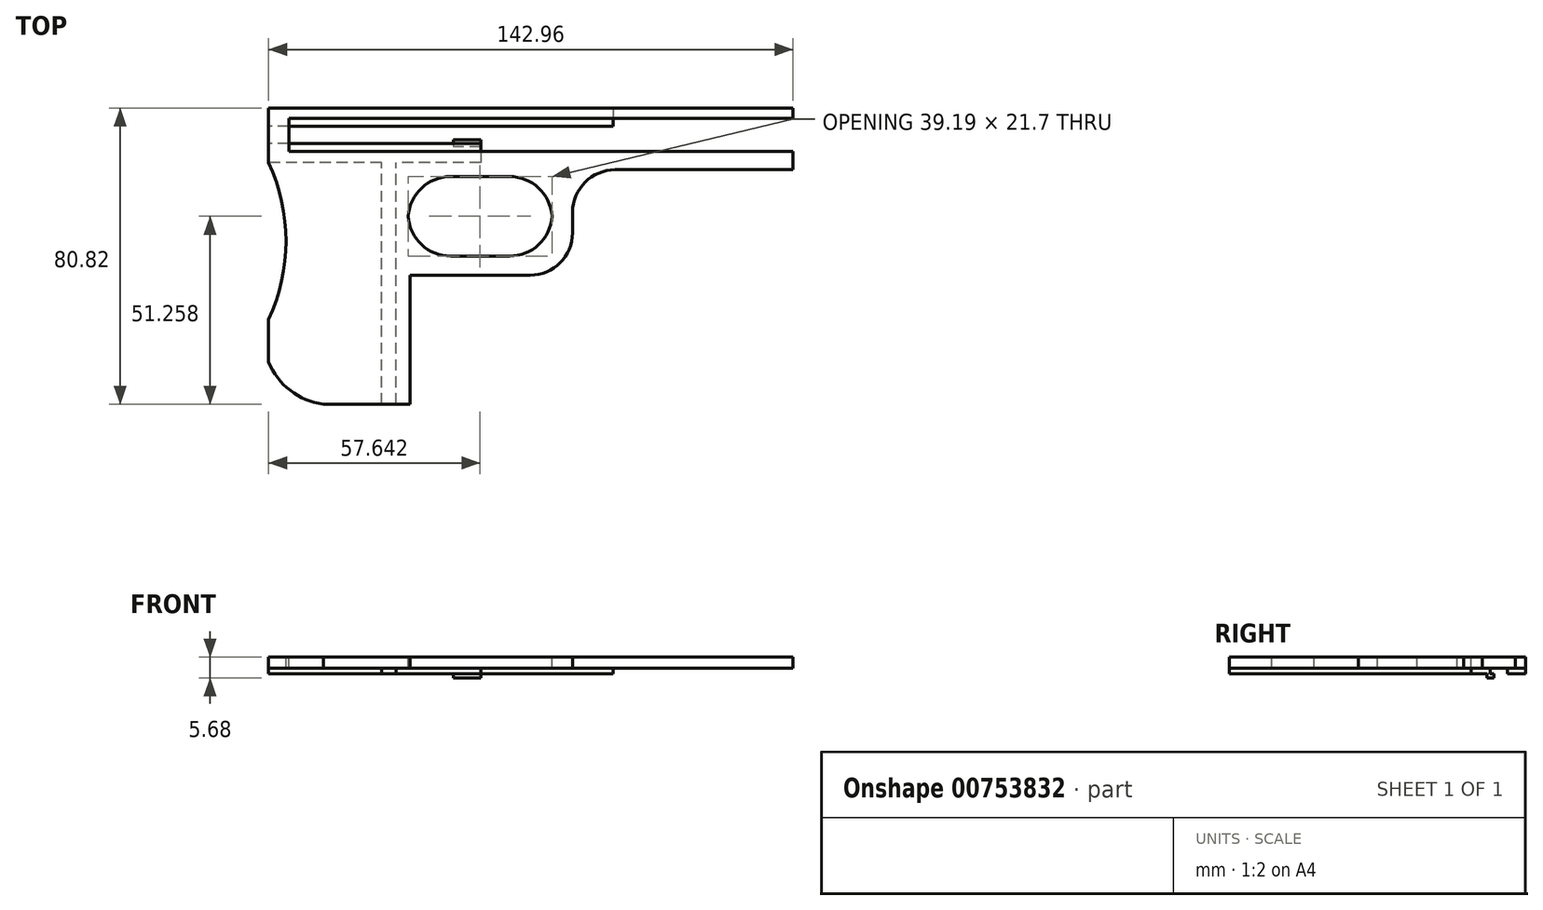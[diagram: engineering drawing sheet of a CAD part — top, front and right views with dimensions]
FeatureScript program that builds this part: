
annotation { "Feature Type Name" : "Feature", "Feature Type Description" : "" }
export const myFeature = defineFeature(function(context is Context, id is Id, definition is map)
    precondition{}
    {
        {
            var Q0;
            Q0=qCreatedBy(makeId("Top.planeOp"),FACE);
            var sketch = newSketch(context, id + "F0", { "sketchPlane" : qUnion([Q0])});
            skLineSegment(sketch, "E0.bottom", {"start": v(-71.48, -40.4) * mm, "end": v(71.48, -40.4) * mm});
            skLineSegment(sketch, "E0.top", {"start": v(-71.48, 40.4) * mm, "end": v(71.48, 40.4) * mm});
            skLineSegment(sketch, "E0.left", {"start": v(-71.48, -40.4) * mm, "end": v(-71.48, 40.4) * mm});
            skLineSegment(sketch, "E0.right", {"start": v(71.48, -40.4) * mm, "end": v(71.48, 40.4) * mm});
            skPoint(sketch, "E0.middle", {"position": v(0, 0) * mm});
            skSolve(sketch);
        }
        {
            var Q0;
            Q0 = qSketchRegion(id + "F0", true);
            extrude(context, id + "F1", {"entities" : qUnion([Q0]), "depth" : 3 * mm, "offsetDistance" : 25 * mm});
        }
        {
            var Q0;
            Q0=makeQuery(id+"F1.opExtrude","CAP_FACE",FACE,{"disambiguationData":[OSD([sQuery(id+"F0.wireOp",EDGE,"E0.bottom"),sQuery(id+"F0.wireOp",EDGE,"E0.top"),sQuery(id+"F0.wireOp",EDGE,"E0.left"),sQuery(id+"F0.wireOp",EDGE,"E0.right")])],"isStart":false});
            var sketch = newSketch(context, id + "F2", { "sketchPlane" : qUnion([Q0])});
            skLineSegment(sketch, "E1.bottom", {"start": v(-65.97, 37.55) * mm, "end": v(71.48, 37.55) * mm});
            skLineSegment(sketch, "E1.top", {"start": v(-65.97, 28.57) * mm, "end": v(71.48, 28.57) * mm});
            skLineSegment(sketch, "E1.left", {"start": v(-65.97, 37.55) * mm, "end": v(-65.97, 28.57) * mm});
            skLineSegment(sketch, "E1.right", {"start": v(71.48, 37.55) * mm, "end": v(71.48, 28.57) * mm});
            skLineSegment(sketch, "E2.bottom", {"start": v(71.48, 23.55) * mm, "end": v(11.39, 23.55) * mm});
            skLineSegment(sketch, "E2.top", {"start": v(71.48, 5.05) * mm, "end": v(11.39, 5.05) * mm});
            skLineSegment(sketch, "E2.left", {"start": v(71.48, 23.55) * mm, "end": v(71.48, 5.05) * mm});
            skLineSegment(sketch, "E2.right", {"start": v(11.39, 23.55) * mm, "end": v(11.39, 5.05) * mm});
            skSolve(sketch);
        }
        {
            var Q0;
            Q0 = qSketchRegion(id + "F2", true);
            extrude(context, id + "F3", {"entities" : qUnion([Q0]), "operationType" : NewBodyOperationType.REMOVE, "oppositeDirection" : true, "depth" : 52.3 * mm, "offsetDistance" : 25 * mm});
        }
        {
            var Q0;
            Q0=makeQuery(id+"F1.opExtrude","CAP_FACE",FACE,{"disambiguationData":[OSD([sQuery(id+"F0.wireOp",EDGE,"E0.bottom"),sQuery(id+"F0.wireOp",EDGE,"E0.top"),sQuery(id+"F0.wireOp",EDGE,"E0.left"),sQuery(id+"F0.wireOp",EDGE,"E0.right")])],"isStart":false});
            var sketch = newSketch(context, id + "F4", { "sketchPlane" : qUnion([Q0])});
            skLineSegment(sketch, "E3.bottom", {"start": v(-33.46, 21.7) * mm, "end": v(5.78, 21.7) * mm});
            skLineSegment(sketch, "E3.top", {"start": v(-33.46, 0) * mm, "end": v(5.78, 0) * mm});
            skLineSegment(sketch, "E3.left", {"start": v(-33.46, 21.7) * mm, "end": v(-33.46, 0) * mm});
            skLineSegment(sketch, "E3.right", {"start": v(5.78, 21.7) * mm, "end": v(5.78, 0) * mm});
            skSolve(sketch);
        }
        {
            var Q0;
            Q0 = qSketchRegion(id + "F4", true);
            extrude(context, id + "F5", {"entities" : qUnion([Q0]), "operationType" : NewBodyOperationType.REMOVE, "oppositeDirection" : true, "depth" : 25 * mm, "offsetDistance" : 25 * mm});
        }
        {
            var Q0;
            Q0=makeQuery(id+"F1.opExtrude","CAP_FACE",FACE,{"disambiguationData":[OSD([sQuery(id+"F0.wireOp",EDGE,"E0.bottom"),sQuery(id+"F0.wireOp",EDGE,"E0.top"),sQuery(id+"F0.wireOp",EDGE,"E0.left"),sQuery(id+"F0.wireOp",EDGE,"E0.right")])],"isStart":false});
            var sketch = newSketch(context, id + "F6", { "sketchPlane" : qUnion([Q0])});
            skLineSegment(sketch, "E4.bottom", {"start": v(13.75, 0) * mm, "end": v(98.67, 0) * mm});
            skLineSegment(sketch, "E4.top", {"start": v(13.75, -55.24) * mm, "end": v(98.67, -55.24) * mm});
            skLineSegment(sketch, "E4.left", {"start": v(13.75, 0) * mm, "end": v(13.75, -55.24) * mm});
            skLineSegment(sketch, "E4.right", {"start": v(98.67, 0) * mm, "end": v(98.67, -55.24) * mm});
            skLineSegment(sketch, "E5.bottom", {"start": v(17.1, -5.2) * mm, "end": v(-27.22, -5.2) * mm});
            skLineSegment(sketch, "E5.top", {"start": v(17.1, -49.97) * mm, "end": v(-27.22, -49.97) * mm});
            skLineSegment(sketch, "E5.left", {"start": v(17.1, -5.2) * mm, "end": v(17.1, -49.97) * mm});
            skLineSegment(sketch, "E5.right", {"start": v(-27.22, -5.2) * mm, "end": v(-27.22, -49.97) * mm});
            skSolve(sketch);
        }
        {
            var Q0;
            Q0 = qSketchRegion(id + "F6", true);
            extrude(context, id + "F7", {"entities" : qUnion([Q0]), "operationType" : NewBodyOperationType.REMOVE, "oppositeDirection" : true, "depth" : 25 * mm, "offsetDistance" : 25 * mm});
        }
        {
            var Q0;
            Q0=makeQuery(id+"F1.opExtrude","CAP_FACE",FACE,{"disambiguationData":[OSD([sQuery(id+"F0.wireOp",EDGE,"E0.bottom"),sQuery(id+"F0.wireOp",EDGE,"E0.top"),sQuery(id+"F0.wireOp",EDGE,"E0.left"),sQuery(id+"F0.wireOp",EDGE,"E0.right")])],"isStart":false});
            var sketch = newSketch(context, id + "F8", { "sketchPlane" : qUnion([Q0])});
            skLineSegment(sketch, "E6.bottom", {"start": v(11.39, 5.05) * mm, "end": v(114, 5.05) * mm});
            skLineSegment(sketch, "E6.top", {"start": v(11.39, -13.38) * mm, "end": v(114, -13.38) * mm});
            skLineSegment(sketch, "E6.left", {"start": v(11.39, 5.05) * mm, "end": v(11.39, -13.38) * mm});
            skLineSegment(sketch, "E6.right", {"start": v(114, 5.05) * mm, "end": v(114, -13.38) * mm});
            skSolve(sketch);
        }
        {
            var Q0;
            Q0 = qSketchRegion(id + "F8", true);
            extrude(context, id + "F9", {"entities" : qUnion([Q0]), "operationType" : NewBodyOperationType.REMOVE, "oppositeDirection" : true, "depth" : 25 * mm, "offsetDistance" : 25 * mm});
        }
        {
            var Q0;
            Q0=makeQuery(id+"F9.boolean.opBoolean","INTERSECT",EDGE,{"derivedFrom":[makeQuery(id+"F7.boolean.opBoolean","COPY",FACE,{"derivedFrom":makeQuery(id+"F7.opExtrude","SWEPT_FACE",FACE,{"disambiguationData":[OSD([sQuery(id+"F6.wireOp",EDGE,"E5.bottom")])]})}),makeQuery(id+"F9.opExtrude","SWEPT_FACE",FACE,{"disambiguationData":[OSD([sQuery(id+"F8.wireOp",EDGE,"E6.left")])]})]});
            var Q1;
            Q1=makeQuery(id+"F3.boolean.opBoolean","COPY",EDGE,{"derivedFrom":makeQuery(id+"F3.opExtrude","SWEPT_EDGE",EDGE,{"disambiguationData":[OSD([sQuery(id+"F2.wireOp",EDGE,"E2.bottom"),sQuery(id+"F2.wireOp",EDGE,"E2.right")])]})});
            var Q2;
            Q2=makeQuery(id+"F7.boolean.opBoolean","COPY",EDGE,{"derivedFrom":makeQuery(id+"F7.opExtrude","SWEPT_EDGE",EDGE,{"disambiguationData":[OSD([sQuery(id+"F6.wireOp",EDGE,"E5.bottom"),sQuery(id+"F6.wireOp",EDGE,"E5.right")])]})});
            var Q3;
            Q3=makeQuery(id+"F5.boolean.opBoolean","COPY",EDGE,{"derivedFrom":makeQuery(id+"F5.opExtrude","SWEPT_EDGE",EDGE,{"disambiguationData":[OSD([sQuery(id+"F4.wireOp",EDGE,"E3.bottom"),sQuery(id+"F4.wireOp",EDGE,"E3.left")])]})});
            var Q4;
            Q4=makeQuery(id+"F5.boolean.opBoolean","COPY",EDGE,{"derivedFrom":makeQuery(id+"F5.opExtrude","SWEPT_EDGE",EDGE,{"disambiguationData":[OSD([sQuery(id+"F4.wireOp",EDGE,"E3.top"),sQuery(id+"F4.wireOp",EDGE,"E3.right")])]})});
            var Q5;
            Q5=makeQuery(id+"F5.boolean.opBoolean","COPY",EDGE,{"derivedFrom":makeQuery(id+"F5.opExtrude","SWEPT_EDGE",EDGE,{"disambiguationData":[OSD([sQuery(id+"F4.wireOp",EDGE,"E3.top"),sQuery(id+"F4.wireOp",EDGE,"E3.left")])]})});
            var Q6;
            Q6=makeQuery(id+"F5.boolean.opBoolean","COPY",EDGE,{"derivedFrom":makeQuery(id+"F5.opExtrude","SWEPT_EDGE",EDGE,{"disambiguationData":[OSD([sQuery(id+"F4.wireOp",EDGE,"E3.bottom"),sQuery(id+"F4.wireOp",EDGE,"E3.right")])]})});
            fillet(context, id + "F10", {"entities" : qUnion([Q0, Q1, Q2, Q3, Q4, Q5, Q6]), "radius" : 11.6 * mm, "tangentPropagation" : true, "allowEdgeOverflow" : false});
        }
        {
            var Q0;
            Q0=makeQuery(id+"F1.opExtrude","CAP_FACE",FACE,{"disambiguationData":[OSD([sQuery(id+"F0.wireOp",EDGE,"E0.bottom"),sQuery(id+"F0.wireOp",EDGE,"E0.top"),sQuery(id+"F0.wireOp",EDGE,"E0.left"),sQuery(id+"F0.wireOp",EDGE,"E0.right")])],"isStart":false});
            var sketch = newSketch(context, id + "F11", { "sketchPlane" : qUnion([Q0])});
            skArc(sketch, "E7", {"start": v(-71.48, -17.3) * mm, "mid": v(-66.77, 4.1) * mm, "end": v(-71.48, 25.5) * mm});
            skSolve(sketch);
        }
        {
            var Q0;
            Q0 = qSketchRegion(id + "F11", true);
            var Q1;
            {var subQ0=sQuery(id+"F11.wireOp",EDGE,"E7");Q1=makeQuery(id+"F11.imprint","IMPRINT",FACE,{"disambiguationData":[TD([[makeQuery(id+"F11.imprint","IMPRINT",EDGE,{"derivedFrom":subQ0}),1.0]])]});}
            extrude(context, id + "F12", {"entities" : qUnion([Q0, Q1]), "operationType" : NewBodyOperationType.REMOVE, "oppositeDirection" : true, "depth" : 25 * mm, "offsetDistance" : 25 * mm});
        }
        {
            var Q0;
            Q0=makeQuery(id+"F1.opExtrude","CAP_FACE",FACE,{"disambiguationData":[OSD([sQuery(id+"F0.wireOp",EDGE,"E0.bottom"),sQuery(id+"F0.wireOp",EDGE,"E0.top"),sQuery(id+"F0.wireOp",EDGE,"E0.left"),sQuery(id+"F0.wireOp",EDGE,"E0.right")])],"isStart":false});
            var sketch = newSketch(context, id + "F13", { "sketchPlane" : qUnion([Q0])});
            skArc(sketch, "E8", {"start": v(-71.48, -28.86) * mm, "mid": v(-63.55, -38.02) * mm, "end": v(-51.66, -40.4) * mm});
            skArc(sketch, "E9", {"start": v(-32.9, -40.4) * mm, "mid": v(-27.36, -33.24) * mm, "end": v(-27.22, -24.18) * mm});
            skArc(sketch, "E10", {"start": v(-21.32, -6.7) * mm, "mid": v(-30.12, -13.47) * mm, "end": v(-27.22, -24.18) * mm});
            skSolve(sketch);
        }
        {
            var Q0;
            {var subQ0=sQuery(id+"F13.wireOp",EDGE,"E10");Q0=makeQuery(id+"F13.imprint","IMPRINT",FACE,{"disambiguationData":[TD([[makeQuery(id+"F13.imprint","IMPRINT",EDGE,{"derivedFrom":subQ0}),1.0]])]});}
            var Q1;
            {var subQ0=sQuery(id+"F13.wireOp",EDGE,"E9");var subQ1=makeQuery(id+"F1.opExtrude","CAP_EDGE",EDGE,{"disambiguationData":[OSD([sQuery(id+"F0.wireOp",EDGE,"E0.bottom")])],"isStart":false});var subQ2=makeQuery(id+"F13.imprint","INTERSECT",VERTEX,{"derivedFrom":[subQ1,subQ0]});Q1=makeQuery(id+"F13.imprint","IMPRINT",FACE,{"disambiguationData":[TD([[makeQuery(id+"F13.imprint","IMPRINT",EDGE,{"disambiguationData":[TD([[subQ2,-1.0]])],"derivedFrom":subQ0}),-1.0]])]});}
            var Q2;
            {var subQ0=sQuery(id+"F13.wireOp",EDGE,"E8");var subQ1=sQuery(id+"F0.wireOp",EDGE,"E0.bottom");var subQ5=makeQuery(id+"F1.opExtrude","CAP_EDGE",EDGE,{"disambiguationData":[OSD([subQ1])],"isStart":false});var subQ6=makeQuery(id+"F13.imprint","INTERSECT",VERTEX,{"disambiguationData":[OD(1.0)],"derivedFrom":[subQ5,subQ0]});Q2=makeQuery(id+"F13.imprint","IMPRINT",FACE,{"disambiguationData":[TD([[makeQuery(id+"F13.imprint","IMPRINT",EDGE,{"disambiguationData":[TD([[subQ6,1.0]])],"derivedFrom":subQ0}),-1.0]])]});}
            extrude(context, id + "F14", {"entities" : qUnion([Q0, Q1, Q2]), "operationType" : NewBodyOperationType.REMOVE, "oppositeDirection" : true, "depth" : 25 * mm, "offsetDistance" : 25 * mm});
        }
        {
            var Q0;
            Q0=makeQuery(id+"F1.opExtrude","CAP_FACE",FACE,{"disambiguationData":[OSD([sQuery(id+"F0.wireOp",EDGE,"E0.bottom"),sQuery(id+"F0.wireOp",EDGE,"E0.top"),sQuery(id+"F0.wireOp",EDGE,"E0.left"),sQuery(id+"F0.wireOp",EDGE,"E0.right")])],"isStart":false});
            var sketch = newSketch(context, id + "F15", { "sketchPlane" : qUnion([Q0])});
            skLineSegment(sketch, "E11", {"start": v(-32.9, -40.4) * mm, "end": v(-32.9, -5.2) * mm});
            skPoint(sketch, "E11.endSnap0", {"position": v(-7.92, -5.2) * mm});
            skLineSegment(sketch, "E12", {"start": v(-32.9, -5.2) * mm, "end": v(-7.92, -5.2) * mm});
            skSolve(sketch);
        }
        {
            var Q0;
            {var subQ3=sQuery(id+"F15.wireOp",EDGE,"E11");Q0=makeQuery(id+"F15.imprint","IMPRINT",FACE,{"disambiguationData":[TD([[makeQuery(id+"F15.imprint","IMPRINT",EDGE,{"derivedFrom":subQ3}),-1.0]])]});}
            extrude(context, id + "F16", {"entities" : qUnion([Q0]), "operationType" : NewBodyOperationType.REMOVE, "oppositeDirection" : true, "depth" : 25 * mm, "offsetDistance" : 25 * mm});
        }
        {
            var Q0;
            Q0=makeQuery(id+"F1.opExtrude","CAP_FACE",FACE,{"disambiguationData":[OSD([sQuery(id+"F0.wireOp",EDGE,"E0.bottom"),sQuery(id+"F0.wireOp",EDGE,"E0.top"),sQuery(id+"F0.wireOp",EDGE,"E0.left"),sQuery(id+"F0.wireOp",EDGE,"E0.right")])],"isStart":true});
            var sketch = newSketch(context, id + "F17", { "sketchPlane" : qUnion([Q0])});
            skLineSegment(sketch, "E13.bottom", {"start": v(22.44, -40.4) * mm, "end": v(-71.48, -40.4) * mm});
            skLineSegment(sketch, "E13.top", {"start": v(22.44, -35.37) * mm, "end": v(-71.48, -35.37) * mm});
            skLineSegment(sketch, "E13.left", {"start": v(22.44, -40.4) * mm, "end": v(22.44, -35.37) * mm});
            skLineSegment(sketch, "E13.right", {"start": v(-71.48, -40.4) * mm, "end": v(-71.48, -35.37) * mm});
            skSolve(sketch);
        }
        {
            var Q0;
            Q0 = qSketchRegion(id + "F17", true);
            extrude(context, id + "F18", {"entities" : qUnion([Q0]), "operationType" : NewBodyOperationType.ADD, "depth" : 1.48 * mm, "offsetDistance" : 25 * mm});
        }
        {
            var Q0;
            {var subQ9=sQuery(id+"F0.wireOp",EDGE,"E0.left");var subQ11=sQuery(id+"F0.wireOp",EDGE,"E0.right");var subQ12=sQuery(id+"F0.wireOp",EDGE,"E0.bottom");Q0=makeQuery(id+"F18.boolean.opBoolean","SPLIT",FACE,{"disambiguationData":[TD([makeQuery(id+"F1.opExtrude","SWEPT_FACE",FACE,{"disambiguationData":[OSD([subQ12])]})])],"derivedFrom":makeQuery(id+"F1.opExtrude","CAP_FACE",FACE,{"disambiguationData":[OSD([subQ12,sQuery(id+"F0.wireOp",EDGE,"E0.top"),subQ9,subQ11])],"isStart":true})});}
            var sketch = newSketch(context, id + "F19", { "sketchPlane" : qUnion([Q0])});
            skLineSegment(sketch, "E14.bottom", {"start": v(-13.69, -30.76) * mm, "end": v(-71.48, -30.76) * mm});
            skLineSegment(sketch, "E14.top", {"start": v(-13.69, -25.5) * mm, "end": v(-71.48, -25.5) * mm});
            skLineSegment(sketch, "E14.left", {"start": v(-13.69, -30.76) * mm, "end": v(-13.69, -25.5) * mm});
            skLineSegment(sketch, "E14.right", {"start": v(-71.48, -30.76) * mm, "end": v(-71.48, -25.5) * mm});
            skSolve(sketch);
        }
        {
            var Q0;
            {var subQ0=sQuery(id+"F19.wireOp",EDGE,"E14.left");var subQ1=sQuery(id+"F19.wireOp",EDGE,"E14.bottom");var subQ2=makeQuery(id+"F19.imprint","INTERSECT",VERTEX,{"derivedFrom":[subQ1,subQ0]});Q0=makeQuery(id+"F19.imprint","IMPRINT",FACE,{"disambiguationData":[TD([[makeQuery(id+"F19.imprint","IMPRINT",EDGE,{"disambiguationData":[TD([[subQ2,-1.0]])],"derivedFrom":subQ0}),1.0]])]});}
            var Q1;
            {var subQ2=sQuery(id+"F19.wireOp",EDGE,"E14.top");Q1=makeQuery(id+"F19.imprint","IMPRINT",FACE,{"disambiguationData":[TD([[makeQuery(id+"F19.imprint","IMPRINT",EDGE,{"derivedFrom":subQ2}),1.0]])]});}
            extrude(context, id + "F20", {"entities" : qUnion([Q0, Q1]), "operationType" : NewBodyOperationType.ADD, "depth" : 0.83 * mm, "offsetDistance" : 25 * mm});
        }
        {
            var Q0;
            Q0=makeQuery(id+"F20.opExtrude","CAP_FACE",FACE,{"disambiguationData":[OSD([sQuery(id+"F19.wireOp",EDGE,"E14.bottom"),sQuery(id+"F19.wireOp",EDGE,"E14.top"),sQuery(id+"F19.wireOp",EDGE,"E14.left"),sQuery(id+"F19.wireOp",EDGE,"E14.right")])],"isStart":false});
            extrude(context, id + "F21", {"entities" : qUnion([Q0]), "operationType" : NewBodyOperationType.ADD, "depth" : 0.73 * mm, "offsetDistance" : 25 * mm});
        }
        {
            var Q0;
            {var subQ0=sQuery(id+"F19.wireOp",EDGE,"E14.top");Q0=makeQuery(id+"F21.boolean.opBoolean","MERGE",FACE,{"derivedFrom":[makeQuery(id+"F20.opExtrude","SWEPT_FACE",FACE,{"disambiguationData":[OSD([subQ0])]}),makeQuery(id+"F21.opExtrude","SWEPT_FACE",FACE,{"disambiguationData":[OSD([subQ0])]})]});}
            var sketch = newSketch(context, id + "F22", { "sketchPlane" : qUnion([Q0])});
            skLineSegment(sketch, "E15.bottom", {"start": v(-36.75, -1.56) * mm, "end": v(-40.74, -1.56) * mm});
            skLineSegment(sketch, "E15.top", {"start": v(-36.75, 0) * mm, "end": v(-40.74, 0) * mm});
            skLineSegment(sketch, "E15.left", {"start": v(-36.75, -1.56) * mm, "end": v(-36.75, 0) * mm});
            skLineSegment(sketch, "E15.right", {"start": v(-40.74, -1.56) * mm, "end": v(-40.74, 0) * mm});
            skSolve(sketch);
        }
        {
            var Q0;
            Q0 = qSketchRegion(id + "F22", true);
            extrude(context, id + "F23", {"entities" : qUnion([Q0]), "operationType" : NewBodyOperationType.ADD, "depth" : 65.89 * mm, "offsetDistance" : 25 * mm});
        }
        {
            var Q0;
            Q0=makeQuery(id+"F23.boolean.opBoolean","MERGE",FACE,{"derivedFrom":[makeQuery(id+"F21.opExtrude","CAP_FACE",FACE,{"disambiguationData":[OSD([sQuery(id+"F19.wireOp",EDGE,"E14.bottom"),sQuery(id+"F19.wireOp",EDGE,"E14.top"),sQuery(id+"F19.wireOp",EDGE,"E14.left"),sQuery(id+"F19.wireOp",EDGE,"E14.right")])],"isStart":false}),makeQuery(id+"F23.opExtrude","SWEPT_FACE",FACE,{"disambiguationData":[OSD([sQuery(id+"F22.wireOp",EDGE,"E15.bottom")])]})]});
            var sketch = newSketch(context, id + "F24", { "sketchPlane" : qUnion([Q0])});
            skLineSegment(sketch, "E16.bottom", {"start": v(-13.69, -31.78) * mm, "end": v(-21.1, -31.78) * mm});
            skLineSegment(sketch, "E16.top", {"start": v(-13.69, -29.8) * mm, "end": v(-21.1, -29.8) * mm});
            skLineSegment(sketch, "E16.left", {"start": v(-13.69, -31.78) * mm, "end": v(-13.69, -29.8) * mm});
            skLineSegment(sketch, "E16.right", {"start": v(-21.1, -31.78) * mm, "end": v(-21.1, -29.8) * mm});
            skSolve(sketch);
        }
        {
            var Q0;
            Q0 = qSketchRegion(id + "F24", true);
            extrude(context, id + "F25", {"entities" : qUnion([Q0]), "operationType" : NewBodyOperationType.ADD, "depth" : 1.12 * mm, "offsetDistance" : 25 * mm});
        }
    });
